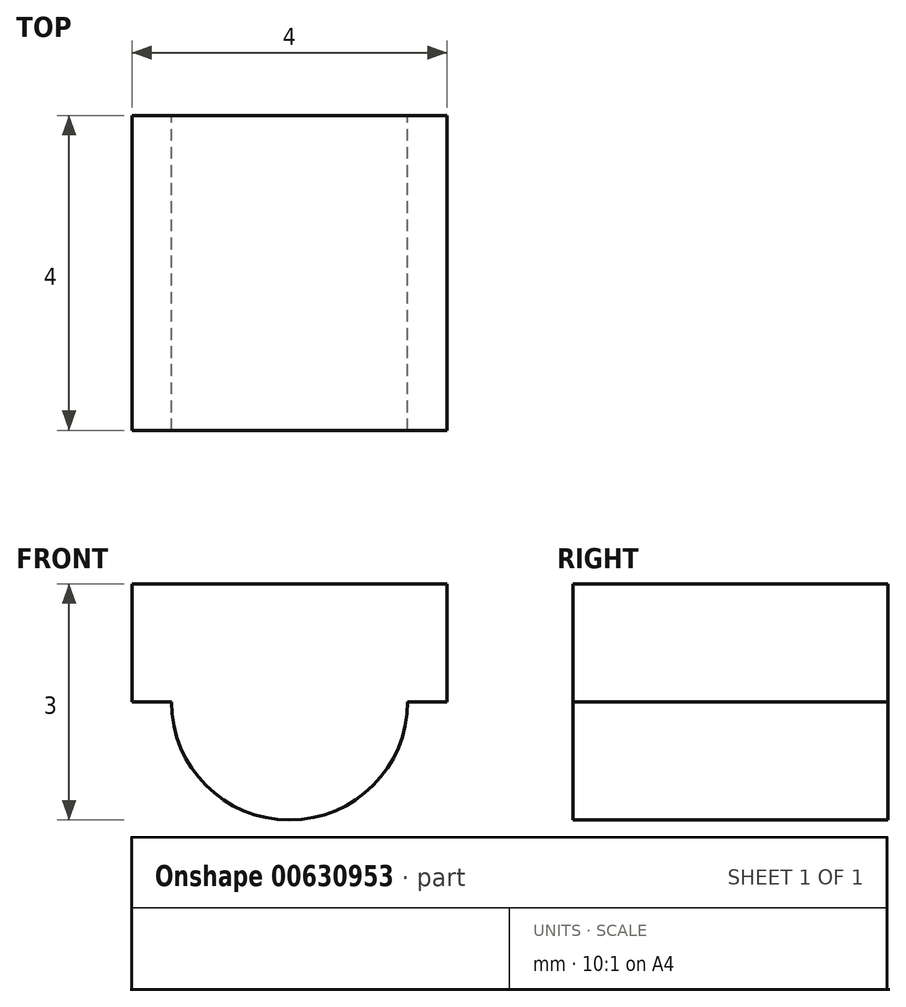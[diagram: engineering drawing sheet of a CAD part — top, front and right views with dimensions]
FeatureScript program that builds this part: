
annotation { "Feature Type Name" : "Feature", "Feature Type Description" : "" }
export const myFeature = defineFeature(function(context is Context, id is Id, definition is map)
    precondition{}
    {
        {
            var Q0;
            Q0=qCreatedBy(makeId("Front.planeOp"),FACE);
            var sketch = newSketch(context, id + "F0", { "sketchPlane" : qUnion([Q0])});
            skCircle(sketch, "E0", {"center": v(0, 0) * mm, "radius": 1.5 * mm});
            skSolve(sketch);
        }
        {
            var Q0;
            Q0 = qSketchRegion(id + "F0", true);
            extrude(context, id + "F1", {"entities" : qUnion([Q0]), "depth" : 4 * mm, "offsetDistance" : 25 * mm});
        }
        {
            var Q0;
            Q0=qCreatedBy(makeId("Top.planeOp"),FACE);
            var sketch = newSketch(context, id + "F2", { "sketchPlane" : qUnion([Q0])});
            skLineSegment(sketch, "E1.bottom", {"start": v(0, 0) * mm, "end": v(2, 0) * mm});
            skLineSegment(sketch, "E1.left", {"start": v(0, 0) * mm, "end": v(0, -3) * mm});
            skLineSegment(sketch, "E2", {"start": v(0, 0) * mm, "end": v(0, -7.8) * mm, "construction": true});
            skLineSegment(sketch, "E3.0", {"start": v(1.5, -4) * mm, "end": v(-1.5, -4) * mm, "construction": true});
            skPoint(sketch, "E4", {"position": v(0, -4) * mm});
            skLineSegment(sketch, "E5", {"start": v(0, -4) * mm, "end": v(2, -4) * mm});
            skLineSegment(sketch, "E6", {"start": v(2, 0) * mm, "end": v(2, -4) * mm});
            skLineSegment(sketch, "E7", {"start": v(0, -4) * mm, "end": v(0, 0.08) * mm});
            skPoint(sketch, "E7.endSnap0", {"position": v(0, -3.9) * mm});
            skLineSegment(sketch, "E8.MirrorCS", {"start": v(0, -4) * mm, "end": v(-2, -4) * mm});
            skLineSegment(sketch, "E9.MirrorCS", {"start": v(-2, 0) * mm, "end": v(-2, -4) * mm});
            skLineSegment(sketch, "E10.MirrorCS", {"start": v(0, 0) * mm, "end": v(-2, 0) * mm});
            skSolve(sketch);
        }
        {
            var Q0;
            Q0 = qSketchRegion(id + "F2", true);
            extrude(context, id + "F3", {"entities" : qUnion([Q0]), "operationType" : NewBodyOperationType.ADD, "depth" : 1.5 * mm, "offsetDistance" : 25 * mm});
        }
    });
